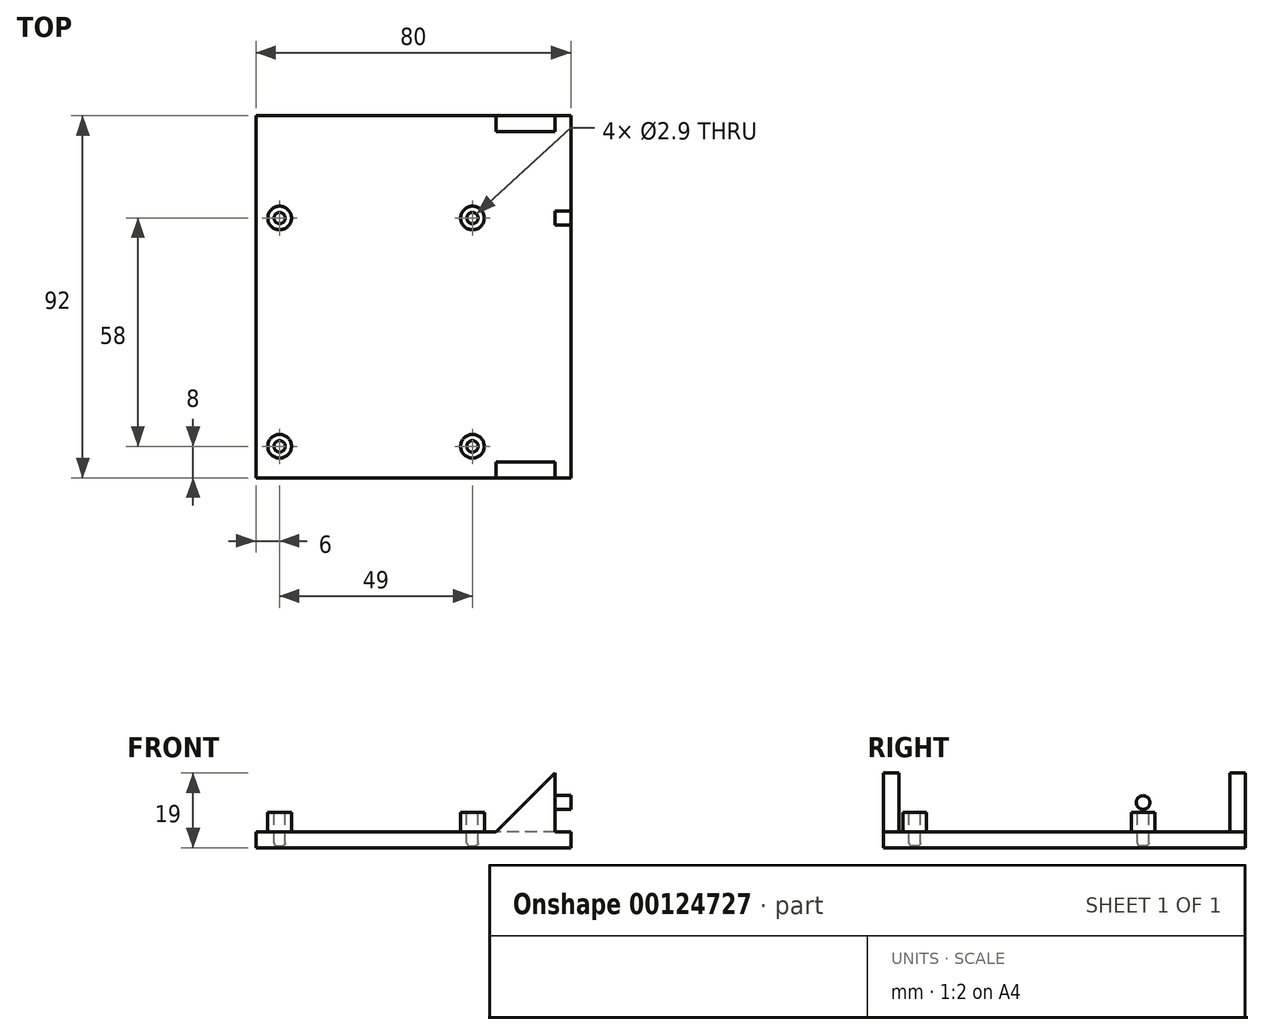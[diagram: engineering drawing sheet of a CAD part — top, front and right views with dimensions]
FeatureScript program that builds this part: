
annotation { "Feature Type Name" : "Feature", "Feature Type Description" : "" }
export const myFeature = defineFeature(function(context is Context, id is Id, definition is map)
    precondition{}
    {
        {
            var Q0;
            Q0=qCreatedBy(makeId("Top.planeOp"),FACE);
            var sketch = newSketch(context, id + "F0", { "sketchPlane" : qUnion([Q0])});
            skLineSegment(sketch, "E0.rect.bottom", {"start": v(40, 46) * mm, "end": v(-40, 46) * mm});
            skLineSegment(sketch, "E0.rect.top", {"start": v(40, -46) * mm, "end": v(-40, -46) * mm});
            skLineSegment(sketch, "E0.rect.left", {"start": v(40, 46) * mm, "end": v(40, -46) * mm});
            skLineSegment(sketch, "E0.rect.right", {"start": v(-40, 46) * mm, "end": v(-40, -46) * mm});
            skPoint(sketch, "E0.rect.middle", {"position": v(0, 0) * mm});
            skSolve(sketch);
        }
        {
            var Q0;
            Q0=qSketchRegion(id+"F0",true);
            extrude(context, id + "F1", {"entities" : qUnion([Q0]), "oppositeDirection" : true, "depth" : 4 * mm});
        }
        {
            var Q0;
            Q0=makeQuery(id+"F1.opExtrude","CAP_FACE",FACE,{"disambiguationData":[OSD([sQuery(id+"F0.wireOp",EDGE,"E0.rect.bottom"),sQuery(id+"F0.wireOp",EDGE,"E0.rect.top"),sQuery(id+"F0.wireOp",EDGE,"E0.rect.left"),sQuery(id+"F0.wireOp",EDGE,"E0.rect.right")])],"isStart":true});
            var sketch = newSketch(context, id + "F2", { "sketchPlane" : qUnion([Q0])});
            skLineSegment(sketch, "E1.rect.bottom", {"start": v(18.5, 46) * mm, "end": v(-37.5, 46) * mm, "construction": true});
            skLineSegment(sketch, "E1.rect.top", {"start": v(18.5, -46) * mm, "end": v(-37.5, -46) * mm, "construction": true});
            skLineSegment(sketch, "E1.rect.left", {"start": v(18.5, 46) * mm, "end": v(18.5, -46) * mm, "construction": true});
            skLineSegment(sketch, "E1.rect.right", {"start": v(-37.5, 46) * mm, "end": v(-37.5, -46) * mm, "construction": true});
            skPoint(sketch, "E1.rect.middle", {"position": v(0, 0) * mm});
            skLineSegment(sketch, "E2.bottom", {"start": v(-34, -38) * mm, "end": v(15, -38) * mm, "construction": true});
            skLineSegment(sketch, "E2.top", {"start": v(-34, 20) * mm, "end": v(15, 20) * mm, "construction": true});
            skLineSegment(sketch, "E2.left", {"start": v(-34, -38) * mm, "end": v(-34, 20) * mm, "construction": true});
            skLineSegment(sketch, "E2.right", {"start": v(15, -38) * mm, "end": v(15, 20) * mm, "construction": true});
            skLineSegment(sketch, "E3", {"start": v(-9.5, -38) * mm, "end": v(-9.5, -46) * mm});
            skSolve(sketch);
        }
        {
            var Q0;
            Q0=makeQuery(id+"F2.imprint","IMPRINT",FACE,{"disambiguationData":[TD([[makeQuery(id+"F2.imprint","IMPRINT",EDGE,{"derivedFrom":makeQuery(id+"F1.opExtrude","CAP_EDGE",EDGE,{"disambiguationData":[OSD([sQuery(id+"F0.wireOp",EDGE,"E0.rect.bottom")])],"isStart":true})}),1.0]])]});
            var sketch = newSketch(context, id + "F3", { "sketchPlane" : qUnion([Q0])});
            skCircle(sketch, "E4", {"center": v(-34, 20) * mm, "radius": 3 * mm});
            skCircle(sketch, "E5", {"center": v(15, 20) * mm, "radius": 3 * mm});
            skCircle(sketch, "E6", {"center": v(15, -38) * mm, "radius": 3 * mm});
            skCircle(sketch, "E7", {"center": v(-34, -38) * mm, "radius": 3 * mm});
            skSolve(sketch);
        }
        {
            var Q0;
            Q0=qSketchRegion(id+"F3",true);
            extrude(context, id + "F4", {"entities" : qUnion([Q0]), "operationType" : NewBodyOperationType.ADD, "depth" : 5 * mm});
        }
        {
            var Q0;
            Q0=makeQuery(id+"F1.opExtrude","CAP_FACE",FACE,{"disambiguationData":[OSD([sQuery(id+"F0.wireOp",EDGE,"E0.rect.bottom"),sQuery(id+"F0.wireOp",EDGE,"E0.rect.top"),sQuery(id+"F0.wireOp",EDGE,"E0.rect.left"),sQuery(id+"F0.wireOp",EDGE,"E0.rect.right")])],"isStart":false});
            cPlane(context, id + "F5", {"entities" : qUnion([Q0]), "cplaneType" : CPlaneType.OFFSET, "offset" : .5 * mm, "oppositeDirection" : true, "width" : 150 * mm, "height" : 150 * mm});
        }
        {
            var Q0;
            Q0=makeQuery(id+"F4.opExtrude","CAP_FACE",FACE,{"disambiguationData":[OSD([sQuery(id+"F3.wireOp",EDGE,"E4")])],"isStart":false});
            var sketch = newSketch(context, id + "F6", { "sketchPlane" : qUnion([Q0])});
            skCircle(sketch, "E8", {"center": v(-34, 20) * mm, "radius": 1.45 * mm});
            skCircle(sketch, "E9", {"center": v(15, 20) * mm, "radius": 1.45 * mm});
            skCircle(sketch, "E10", {"center": v(15, -38) * mm, "radius": 1.45 * mm});
            skCircle(sketch, "E11", {"center": v(-34, -38) * mm, "radius": 1.45 * mm});
            skSolve(sketch);
        }
        {
            var Q0;
            Q0=qSketchRegion(id+"F6",true);
            var Q1;
            Q1=qCreatedBy(id+"F5.planeOp",FACE);
            extrude(context, id + "F7", {"entities" : qUnion([Q0]), "operationType" : NewBodyOperationType.REMOVE, "endBound" : BoundingType.UP_TO_SURFACE, "oppositeDirection" : true, "endBoundEntityFace" : qUnion([Q1]), "depth" : 4.5 * mm});
        }
        {
            var Q0;
            Q0=makeQuery(id+"F4.opExtrude","CAP_EDGE",EDGE,{"disambiguationData":[OSD([sQuery(id+"F3.wireOp",EDGE,"E6")])],"isStart":true});
            var Q1;
            Q1=makeQuery(id+"F4.opExtrude","CAP_EDGE",EDGE,{"disambiguationData":[OSD([sQuery(id+"F3.wireOp",EDGE,"E7")])],"isStart":true});
            var Q2;
            Q2=makeQuery(id+"F4.opExtrude","CAP_EDGE",EDGE,{"disambiguationData":[OSD([sQuery(id+"F3.wireOp",EDGE,"E5")])],"isStart":true});
            var Q3;
            Q3=makeQuery(id+"F4.opExtrude","CAP_EDGE",EDGE,{"disambiguationData":[OSD([sQuery(id+"F3.wireOp",EDGE,"E4")])],"isStart":true});
            var Q4;
            Q4=makeQuery(id+"F7.boolean.opBoolean","COPY",FACE,{"derivedFrom":makeQuery(id+"F7.opExtrude","CAP_FACE",FACE,{"disambiguationData":[OSD([sQuery(id+"F6.wireOp",EDGE,"E10")])],"isStart":false})});
            var Q5;
            Q5=makeQuery(id+"F7.boolean.opBoolean","COPY",EDGE,{"derivedFrom":makeQuery(id+"F7.opExtrude","CAP_EDGE",EDGE,{"disambiguationData":[OSD([sQuery(id+"F6.wireOp",EDGE,"E11")])],"isStart":false})});
            var Q6;
            Q6=makeQuery(id+"F7.boolean.opBoolean","COPY",EDGE,{"derivedFrom":makeQuery(id+"F7.opExtrude","CAP_EDGE",EDGE,{"disambiguationData":[OSD([sQuery(id+"F6.wireOp",EDGE,"E8")])],"isStart":false})});
            var Q7;
            Q7=makeQuery(id+"F7.boolean.opBoolean","COPY",EDGE,{"derivedFrom":makeQuery(id+"F7.opExtrude","CAP_EDGE",EDGE,{"disambiguationData":[OSD([sQuery(id+"F6.wireOp",EDGE,"E9")])],"isStart":false})});
            fillet(context, id + "F8", {"entities" : qUnion([Q0, Q1, Q2, Q3, Q4, Q5, Q6, Q7]), "radius" : .75 * mm, "allowEdgeOverflow" : false});
        }
        {
            var Q0;
            Q0=makeQuery(id+"F1.opExtrude","CAP_FACE",FACE,{"disambiguationData":[OSD([sQuery(id+"F0.wireOp",EDGE,"E0.rect.bottom"),sQuery(id+"F0.wireOp",EDGE,"E0.rect.top"),sQuery(id+"F0.wireOp",EDGE,"E0.rect.left"),sQuery(id+"F0.wireOp",EDGE,"E0.rect.right")])],"isStart":true});
            var sketch = newSketch(context, id + "F9", { "sketchPlane" : qUnion([Q0])});
            skLineSegment(sketch, "E12.bottom", {"start": v(40, 46) * mm, "end": v(36, 46) * mm});
            skLineSegment(sketch, "E12.top", {"start": v(40, -46) * mm, "end": v(36, -46) * mm});
            skLineSegment(sketch, "E12.left", {"start": v(40, 46) * mm, "end": v(40, -46) * mm});
            skLineSegment(sketch, "E12.right", {"start": v(36, 46) * mm, "end": v(36, -46) * mm});
            skSolve(sketch);
        }
        {
            var Q0;
            Q0=makeQuery(id+"F9.imprint","IMPRINT",FACE,{"disambiguationData":[TD([[makeQuery(id+"F9.imprint","IMPRINT",EDGE,{"derivedFrom":sQuery(id+"F9.wireOp",EDGE,"E12.bottom")}),1.0]])]});
            extrude(context, id + "F10", {"entities" : qUnion([Q0]), "operationType" : NewBodyOperationType.ADD, "depth" : 15 * mm});
        }
        {
            var Q0;
            Q0=makeQuery(id+"F10.opExtrude","SWEPT_FACE",FACE,{"disambiguationData":[OSD([sQuery(id+"F9.wireOp",EDGE,"E12.right")])]});
            var sketch = newSketch(context, id + "F11", { "sketchPlane" : qUnion([Q0])});
            skLineSegment(sketch, "E13", {"start": v(-46, 7.5) * mm, "end": v(46, 7.5) * mm, "construction": true});
            skCircle(sketch, "E14", {"center": v(22, 7.5) * mm, "radius": 1.75 * mm});
            skLineSegment(sketch, "E15", {"start": v(0, 0) * mm, "end": v(0, 15) * mm, "construction": true});
            skCircle(sketch, "E16.MirrorC", {"center": v(-20, 7.5) * mm, "radius": 1.75 * mm});
            skSolve(sketch);
        }
        {
            var Q0;
            Q0=makeQuery(id+"F11.imprint","IMPRINT",FACE,{"disambiguationData":[TD([[makeQuery(id+"F11.imprint","IMPRINT",EDGE,{"derivedFrom":sQuery(id+"F11.wireOp",EDGE,"E16.MirrorC")}),-1.0]])]});
            var Q1;
            Q1=makeQuery(id+"F11.imprint","IMPRINT",FACE,{"disambiguationData":[TD([[makeQuery(id+"F11.imprint","IMPRINT",EDGE,{"derivedFrom":sQuery(id+"F11.wireOp",EDGE,"E14")}),1.0]])]});
            var Q2;
            Q2=makeQuery(id+"F10.boolean.opBoolean","MERGE",FACE,{"derivedFrom":[makeQuery(id+"FyLrYfBwNOMBecb_1.boolean.opBoolean","MERGE",FACE,{"derivedFrom":[makeQuery(id+"F1.opExtrude","SWEPT_FACE",FACE,{"disambiguationData":[OSD([sQuery(id+"F0.wireOp",EDGE,"E0.rect.left")])]}),makeQuery(id+"FyLrYfBwNOMBecb_1.opExtrude","SWEPT_FACE",FACE,{"disambiguationData":[OSD([sQuery(id+"F1auum0bioTXr5n_1.wireOp",EDGE,"c4674b5a-09ab-453d-9263-ba86ed64be00.left")])]})]}),makeQuery(id+"F10.opExtrude","SWEPT_FACE",FACE,{"disambiguationData":[OSD([sQuery(id+"F9.wireOp",EDGE,"E12.left")])]})]});
            extrude(context, id + "F12", {"entities" : qUnion([Q0, Q1]), "operationType" : NewBodyOperationType.REMOVE, "endBound" : BoundingType.UP_TO_SURFACE, "oppositeDirection" : true, "endBoundEntityFace" : qUnion([Q2]), "depth" : 25 * mm});
        }
        {
            var Q0;
            Q0=makeQuery(id+"F10.boolean.opBoolean","MERGE",FACE,{"derivedFrom":[makeQuery(id+"F1.opExtrude","SWEPT_FACE",FACE,{"disambiguationData":[OSD([sQuery(id+"F0.wireOp",EDGE,"E0.rect.bottom")])]}),makeQuery(id+"F10.opExtrude","SWEPT_FACE",FACE,{"disambiguationData":[OSD([sQuery(id+"F9.wireOp",EDGE,"E12.bottom")])]})]});
            var sketch = newSketch(context, id + "F13", { "sketchPlane" : qUnion([Q0])});
            skLineSegment(sketch, "E17", {"start": v(-36, 15) * mm, "end": v(-21, 0) * mm});
            skLineSegment(sketch, "E18", {"start": v(-21, 0) * mm, "end": v(-36, 0) * mm});
            skLineSegment(sketch, "E19", {"start": v(-36, 0) * mm, "end": v(-36, 15) * mm});
            skSolve(sketch);
        }
        {
            var Q0;
            Q0=makeQuery(id+"F13.imprint","IMPRINT",FACE,{"disambiguationData":[TD([[makeQuery(id+"F13.imprint","IMPRINT",EDGE,{"derivedFrom":sQuery(id+"F13.wireOp",EDGE,"E17")}),-1.0]])]});
            extrude(context, id + "F14", {"entities" : qUnion([Q0]), "operationType" : NewBodyOperationType.ADD, "oppositeDirection" : true, "depth" : 4 * mm});
        }
        {
            var Q0;
            Q0=makeQuery(id+"F10.boolean.opBoolean","MERGE",FACE,{"derivedFrom":[makeQuery(id+"F1.opExtrude","SWEPT_FACE",FACE,{"disambiguationData":[OSD([sQuery(id+"F0.wireOp",EDGE,"E0.rect.top")])]}),makeQuery(id+"F10.opExtrude","SWEPT_FACE",FACE,{"disambiguationData":[OSD([sQuery(id+"F9.wireOp",EDGE,"E12.top")])]})]});
            var sketch = newSketch(context, id + "F15", { "sketchPlane" : qUnion([Q0])});
            skLineSegment(sketch, "E20", {"start": v(36, 15) * mm, "end": v(21, 0) * mm});
            skLineSegment(sketch, "E21", {"start": v(21, 0) * mm, "end": v(36, 0) * mm});
            skLineSegment(sketch, "E22", {"start": v(36, 0) * mm, "end": v(36, 15) * mm});
            skSolve(sketch);
        }
        {
            var Q0;
            Q0=makeQuery(id+"F15.imprint","IMPRINT",FACE,{"disambiguationData":[TD([[makeQuery(id+"F15.imprint","IMPRINT",EDGE,{"derivedFrom":sQuery(id+"F15.wireOp",EDGE,"E20")}),1.0]])]});
            extrude(context, id + "F16", {"entities" : qUnion([Q0]), "operationType" : NewBodyOperationType.ADD, "oppositeDirection" : true, "depth" : 4 * mm});
        }
    });
